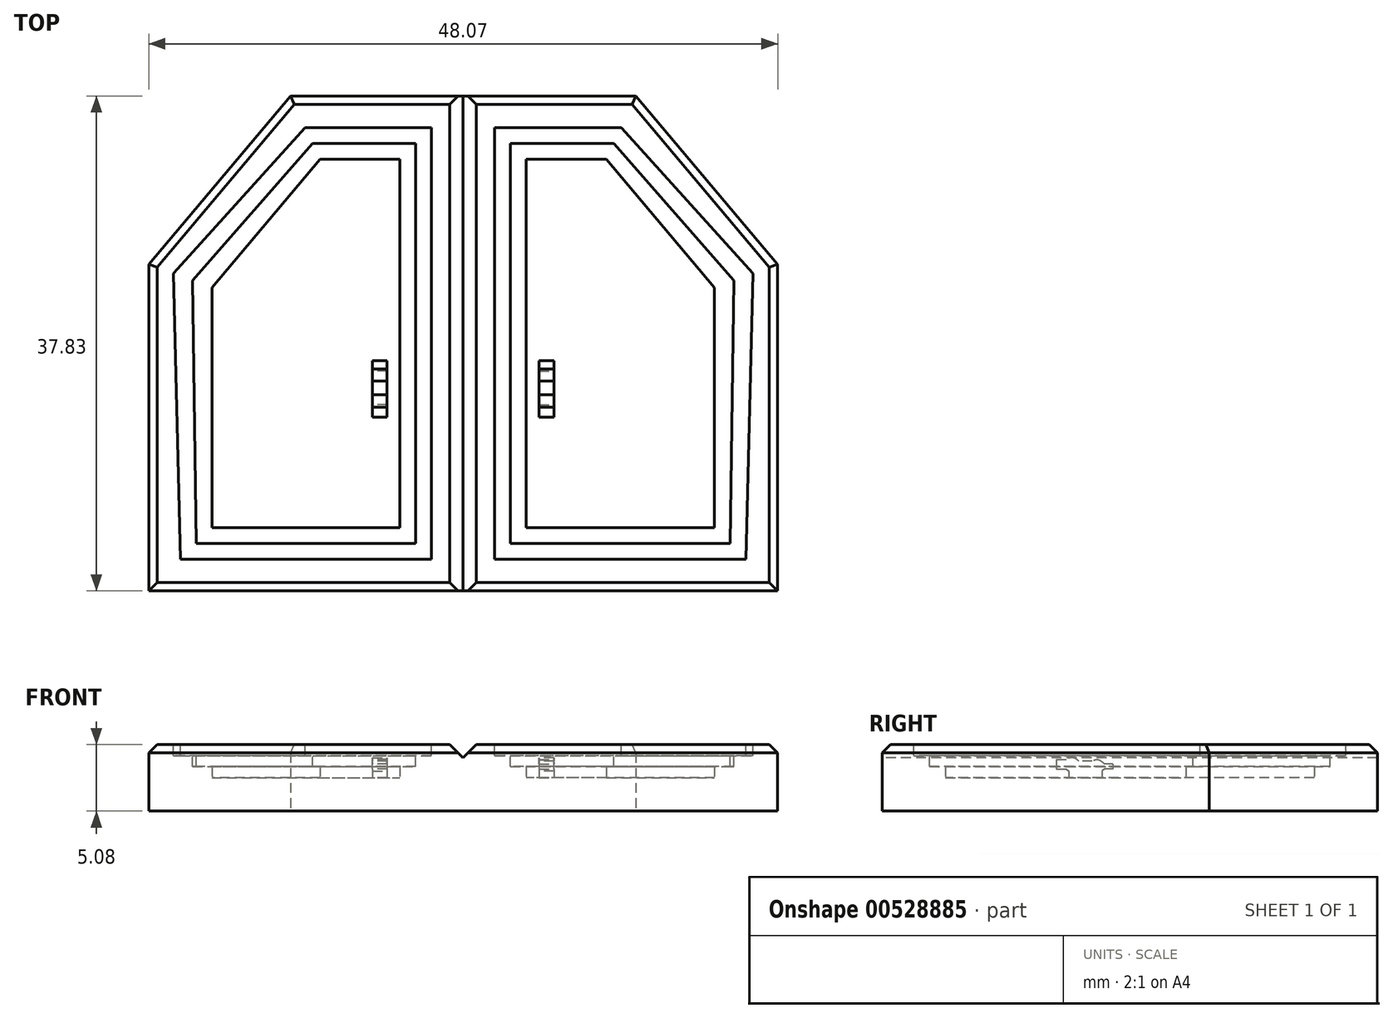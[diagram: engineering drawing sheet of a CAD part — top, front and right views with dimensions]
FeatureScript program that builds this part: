
annotation { "Feature Type Name" : "Feature", "Feature Type Description" : "" }
export const myFeature = defineFeature(function(context is Context, id is Id, definition is map)
    precondition{}
    {
        {
            var Q0;
            Q0=qCreatedBy(makeId("Top.planeOp"),FACE);
            var sketch = newSketch(context, id + "F0", { "sketchPlane" : qUnion([Q0])});
            skLineSegment(sketch, "E0.bottom", {"start": v(-36.19, -42.4) * mm, "end": v(13.77, -42.4) * mm});
            skLineSegment(sketch, "E0.top", {"start": v(-36.19, -4.56) * mm, "end": v(13.77, -4.56) * mm});
            skLineSegment(sketch, "E0.left", {"start": v(-36.19, -42.4) * mm, "end": v(-36.19, -4.56) * mm});
            skLineSegment(sketch, "E0.right", {"start": v(13.77, -42.4) * mm, "end": v(13.77, -4.56) * mm});
            skLineSegment(sketch, "E1", {"start": v(-11.2, -4.56) * mm, "end": v(-11.2, -42.4) * mm});
            skLineSegment(sketch, "E2", {"start": v(-12.16, -4.56) * mm, "end": v(-12.16, -42.4) * mm});
            skLineSegment(sketch, "E3", {"start": v(-25.35, -4.56) * mm, "end": v(-36.19, -17.43) * mm});
            skLineSegment(sketch, "E4", {"start": v(2.23, -4.56) * mm, "end": v(13.77, -17.77) * mm});
            skSolve(sketch);
        }
        {
            var Q0;
            {var subQ0=sQuery(id+"F0.wireOp",EDGE,"E2");Q0=makeQuery(id+"F0.imprint","IMPRINT",FACE,{"disambiguationData":[TD([[makeQuery(id+"F0.imprint","IMPRINT",EDGE,{"derivedFrom":subQ0}),-1.0]])]});}
            var Q1;
            {var subQ4=sQuery(id+"F0.wireOp",EDGE,"E1");Q1=makeQuery(id+"F0.imprint","IMPRINT",FACE,{"disambiguationData":[TD([[makeQuery(id+"F0.imprint","IMPRINT",EDGE,{"derivedFrom":subQ4}),1.0]])]});}
            extrude(context, id + "F1", {"entities" : qUnion([Q0, Q1]), "depth" : 5.08 * mm, "offsetDistance" : 25.4 * mm});
        }
        {
            var Q0;
            Q0=makeQuery(id+"F1.opExtrude","CAP_FACE",FACE,{"disambiguationData":[OSD([sQuery(id+"F0.wireOp",EDGE,"E0.bottom"),sQuery(id+"F0.wireOp",EDGE,"E0.top"),sQuery(id+"F0.wireOp",EDGE,"E0.left"),sQuery(id+"F0.wireOp",EDGE,"E2"),sQuery(id+"F0.wireOp",EDGE,"E3")])],"isStart":false});
            shell(context, id + "F2", {"entities" : qUnion([Q0]), "thickness" : 4.83 * mm});
        }
        {
            var Q0;
            Q0=makeQuery(id+"F2.opShell","OFFSET_FACE",FACE,{"disambiguationData":[OSD([sQuery(id+"F0.wireOp",EDGE,"E0.bottom"),sQuery(id+"F0.wireOp",EDGE,"E0.top"),sQuery(id+"F0.wireOp",EDGE,"E0.left"),sQuery(id+"F0.wireOp",EDGE,"E2"),sQuery(id+"F0.wireOp",EDGE,"E3")])]});
            extrude(context, id + "F3", {"entities" : qUnion([Q0]), "operationType" : NewBodyOperationType.REMOVE, "oppositeDirection" : true, "depth" : 2.54 * mm, "offsetDistance" : 25.4 * mm});
        }
        {
            var Q0;
            Q0=makeQuery(id+"F1.opExtrude","CAP_FACE",FACE,{"disambiguationData":[OSD([sQuery(id+"F0.wireOp",EDGE,"E0.bottom"),sQuery(id+"F0.wireOp",EDGE,"E0.top"),sQuery(id+"F0.wireOp",EDGE,"E0.left"),sQuery(id+"F0.wireOp",EDGE,"E2"),sQuery(id+"F0.wireOp",EDGE,"E3")])],"isStart":false});
            var sketch = newSketch(context, id + "F4", { "sketchPlane" : qUnion([Q0])});
            skLineSegment(sketch, "E5", {"start": v(-33.77, -39.98) * mm, "end": v(-14.57, -39.98) * mm});
            skLineSegment(sketch, "E6", {"start": v(-14.57, -39.98) * mm, "end": v(-14.57, -6.97) * mm});
            skLineSegment(sketch, "E7", {"start": v(-14.57, -6.97) * mm, "end": v(-24.22, -6.97) * mm});
            skLineSegment(sketch, "E8", {"start": v(-24.22, -6.97) * mm, "end": v(-34.3, -18.11) * mm});
            skLineSegment(sketch, "E9", {"start": v(-34.3, -18.11) * mm, "end": v(-33.77, -39.98) * mm});
            skSolve(sketch);
        }
        {
            var Q0;
            Q0=makeQuery(id+"F4.imprint","IMPRINT",FACE,{"disambiguationData":[TD([[makeQuery(id+"F4.imprint","IMPRINT",EDGE,{"derivedFrom":sQuery(id+"F4.wireOp",EDGE,"E5")}),1.0]])]});
            extrude(context, id + "F5", {"entities" : qUnion([Q0]), "operationType" : NewBodyOperationType.REMOVE, "oppositeDirection" : true, "depth" : 0.84 * mm, "offsetDistance" : 25.4 * mm});
        }
        {
            var Q0;
            Q0=makeQuery(id+"F5.boolean.opBoolean","COPY",FACE,{"derivedFrom":makeQuery(id+"F5.opExtrude","CAP_FACE",FACE,{"disambiguationData":[OSD([sQuery(id+"F0.wireOp",EDGE,"E0.bottom"),sQuery(id+"F0.wireOp",EDGE,"E0.top"),sQuery(id+"F0.wireOp",EDGE,"E0.left"),sQuery(id+"F0.wireOp",EDGE,"E2"),sQuery(id+"F0.wireOp",EDGE,"E3"),sQuery(id+"F4.wireOp",EDGE,"E5"),sQuery(id+"F4.wireOp",EDGE,"E6"),sQuery(id+"F4.wireOp",EDGE,"E7"),sQuery(id+"F4.wireOp",EDGE,"E8"),sQuery(id+"F4.wireOp",EDGE,"E9")])],"isStart":false})});
            var sketch = newSketch(context, id + "F6", { "sketchPlane" : qUnion([Q0])});
            skLineSegment(sketch, "E10", {"start": v(-23.66, -8.18) * mm, "end": v(-15.78, -8.18) * mm});
            skLineSegment(sketch, "E11", {"start": v(-15.78, -8.18) * mm, "end": v(-15.78, -38.78) * mm});
            skLineSegment(sketch, "E12", {"start": v(-15.78, -38.78) * mm, "end": v(-32.57, -38.78) * mm});
            skLineSegment(sketch, "E13", {"start": v(-32.57, -38.78) * mm, "end": v(-32.83, -18.65) * mm});
            skLineSegment(sketch, "E14", {"start": v(-32.83, -18.65) * mm, "end": v(-23.66, -8.18) * mm});
            skSolve(sketch);
        }
        {
            var Q0;
            Q0=makeQuery(id+"F6.imprint","IMPRINT",FACE,{"disambiguationData":[TD([[makeQuery(id+"F6.imprint","IMPRINT",EDGE,{"derivedFrom":sQuery(id+"F6.wireOp",EDGE,"E10")}),-1.0]])]});
            extrude(context, id + "F7", {"entities" : qUnion([Q0]), "operationType" : NewBodyOperationType.REMOVE, "oppositeDirection" : true, "depth" : 0.84 * mm, "offsetDistance" : 25.4 * mm});
        }
        {
            var Q0;
            Q0=makeQuery(id+"F3.boolean.opBoolean","COPY",FACE,{"derivedFrom":makeQuery(id+"F3.opExtrude","CAP_FACE",FACE,{"disambiguationData":[OSD([sQuery(id+"F0.wireOp",EDGE,"E0.bottom"),sQuery(id+"F0.wireOp",EDGE,"E0.top"),sQuery(id+"F0.wireOp",EDGE,"E0.left"),sQuery(id+"F0.wireOp",EDGE,"E2"),sQuery(id+"F0.wireOp",EDGE,"E3")])],"isStart":false})});
            extrude(context, id + "F8", {"entities" : qUnion([Q0]), "operationType" : NewBodyOperationType.ADD, "depth" : 0.25 * mm, "offsetDistance" : 25.4 * mm});
        }
        {
            var Q0;
            Q0=makeQuery(id+"F8.opExtrude","CAP_FACE",FACE,{"disambiguationData":[OSD([sQuery(id+"F0.wireOp",EDGE,"E0.bottom"),sQuery(id+"F0.wireOp",EDGE,"E0.top"),sQuery(id+"F0.wireOp",EDGE,"E0.left"),sQuery(id+"F0.wireOp",EDGE,"E2"),sQuery(id+"F0.wireOp",EDGE,"E3")])],"isStart":false});
            var sketch = newSketch(context, id + "F9", { "sketchPlane" : qUnion([Q0])});
            skLineSegment(sketch, "E15.bottom", {"start": v(-17.97, -25.6) * mm, "end": v(-19.08, -25.6) * mm});
            skLineSegment(sketch, "E15.top", {"start": v(-17.97, -28.16) * mm, "end": v(-19.08, -28.16) * mm});
            skLineSegment(sketch, "E15.left", {"start": v(-17.97, -25.6) * mm, "end": v(-17.97, -28.16) * mm});
            skLineSegment(sketch, "E15.right", {"start": v(-19.08, -25.6) * mm, "end": v(-19.08, -28.16) * mm});
            skSolve(sketch);
        }
        {
            var Q0;
            Q0=qSketchRegion(id+"F9",true);
            extrude(context, id + "F10", {"entities" : qUnion([Q0]), "operationType" : NewBodyOperationType.ADD, "depth" : 1.27 * mm, "offsetDistance" : 25.4 * mm});
        }
        {
            var Q0;
            Q0=makeQuery(id+"F10.opExtrude","CAP_EDGE",EDGE,{"disambiguationData":[OSD([sQuery(id+"F9.wireOp",EDGE,"E15.bottom")])],"isStart":false});
            var Q1;
            Q1=makeQuery(id+"F10.opExtrude","CAP_EDGE",EDGE,{"disambiguationData":[OSD([sQuery(id+"F9.wireOp",EDGE,"E15.top")])],"isStart":false});
            chamfer(context, id + "F11", {"entities" : qUnion([Q0, Q1]), "width" : 0.76 * mm, "tangentPropagation" : true});
        }
        {
            var Q0;
            Q0=makeQuery(id+"F11.opChamfer","BLEND_FACE",FACE,{"disambiguationData":[OSD([sQuery(id+"F9.wireOp",EDGE,"E15.top")])]});
            extrude(context, id + "F12", {"entities" : qUnion([Q0]), "operationType" : NewBodyOperationType.ADD, "depth" : 0.76 * mm, "offsetDistance" : 25.4 * mm});
        }
        {
            var Q0;
            Q0=makeQuery(id+"F12.opExtrude","CAP_EDGE",EDGE,{"disambiguationData":[OSD([sQuery(id+"F9.wireOp",EDGE,"E15.top")])],"isStart":false});
            chamfer(context, id + "F13", {"entities" : qUnion([Q0]), "width" : 0.5 * mm, "tangentPropagation" : true});
        }
        {
            var Q0;
            Q0=makeQuery(id+"F11.opChamfer","BLEND_FACE",FACE,{"disambiguationData":[OSD([sQuery(id+"F9.wireOp",EDGE,"E15.bottom")])]});
            extrude(context, id + "F14", {"entities" : qUnion([Q0]), "operationType" : NewBodyOperationType.ADD, "depth" : 0.5 * mm, "offsetDistance" : 25.4 * mm});
        }
        {
            var Q0;
            Q0=makeQuery(id+"F14.opExtrude","CAP_EDGE",EDGE,{"disambiguationData":[OSD([sQuery(id+"F9.wireOp",EDGE,"E15.bottom")])],"isStart":false});
            chamfer(context, id + "F15", {"entities" : qUnion([Q0]), "width" : 0.25 * mm, "tangentPropagation" : true});
        }
        {
            var Q0;
            Q0=makeQuery(id+"F15.opChamfer","BLEND_FACE",FACE,{"disambiguationData":[OSD([sQuery(id+"F9.wireOp",EDGE,"E15.bottom")])]});
            extrude(context, id + "F16", {"entities" : qUnion([Q0]), "operationType" : NewBodyOperationType.ADD, "depth" : 0.64 * mm, "offsetDistance" : 25.4 * mm});
        }
        {
            var Q0;
            Q0=makeQuery(id+"F13.opChamfer","BLEND_FACE",FACE,{"disambiguationData":[OSD([sQuery(id+"F9.wireOp",EDGE,"E15.top")])]});
            extrude(context, id + "F17", {"entities" : qUnion([Q0]), "operationType" : NewBodyOperationType.ADD, "depth" : 0.76 * mm, "offsetDistance" : 25.4 * mm});
        }
        {
            var Q0;
            Q0=makeQuery(id+"F12.opExtrude","CAP_EDGE",EDGE,{"disambiguationData":[OSD([sQuery(id+"F9.wireOp",EDGE,"E15.bottom"),sQuery(id+"F9.wireOp",EDGE,"E15.top"),sQuery(id+"F9.wireOp",EDGE,"E15.left"),sQuery(id+"F9.wireOp",EDGE,"E15.right")])],"isStart":false});
            var Q1;
            Q1=makeQuery(id+"F14.opExtrude","CAP_EDGE",EDGE,{"disambiguationData":[OSD([sQuery(id+"F9.wireOp",EDGE,"E15.bottom"),sQuery(id+"F9.wireOp",EDGE,"E15.top"),sQuery(id+"F9.wireOp",EDGE,"E15.left"),sQuery(id+"F9.wireOp",EDGE,"E15.right")])],"isStart":false});
            fillet(context, id + "F18", {"entities" : qUnion([Q0, Q1]), "radius" : 0.64 * mm, "tangentPropagation" : true, "allowEdgeOverflow" : false});
        }
        {
            var Q0;
            Q0=makeQuery(id+"F1.opExtrude","SWEPT_BODY",BODY,{"disambiguationData":[OSD([sQuery(id+"F0.wireOp",EDGE,"E0.bottom"),sQuery(id+"F0.wireOp",EDGE,"E0.top"),sQuery(id+"F0.wireOp",EDGE,"E0.right"),sQuery(id+"F0.wireOp",EDGE,"E1"),sQuery(id+"F0.wireOp",EDGE,"E4")])]});
            deleteBodies(context, id + "F19", {"entities" : qUnion([Q0])});
        }
        {
            var Q0;
            {var subQ0=sQuery(id+"F0.wireOp",EDGE,"E0.top");Q0=makeQuery(id+"F1.opExtrude","CAP_EDGE",EDGE,{"disambiguationData":[OSD([subQ0]),TDD([makeQuery(id+"F0.imprint","IMPRINT",EDGE,{"disambiguationData":[TD([[makeQuery(id+"F0.imprint","INTERSECT",VERTEX,{"derivedFrom":[subQ0,sQuery(id+"F0.wireOp",EDGE,"E2")]}),1.0]])],"derivedFrom":subQ0})])],"isStart":false});}
            var Q1;
            Q1=makeQuery(id+"F1.opExtrude","CAP_EDGE",EDGE,{"disambiguationData":[OSD([sQuery(id+"F0.wireOp",EDGE,"E3")])],"isStart":false});
            var Q2;
            Q2=makeQuery(id+"F1.opExtrude","CAP_EDGE",EDGE,{"disambiguationData":[OSD([sQuery(id+"F0.wireOp",EDGE,"E0.left")])],"isStart":false});
            var Q3;
            {var subQ0=sQuery(id+"F0.wireOp",EDGE,"E0.bottom");Q3=makeQuery(id+"F1.opExtrude","CAP_EDGE",EDGE,{"disambiguationData":[OSD([subQ0]),TDD([makeQuery(id+"F0.imprint","IMPRINT",EDGE,{"disambiguationData":[TD([[makeQuery(id+"F0.imprint","INTERSECT",VERTEX,{"derivedFrom":[subQ0,sQuery(id+"F0.wireOp",EDGE,"E0.left")]}),-1.0]])],"derivedFrom":subQ0})])],"isStart":false});}
            chamfer(context, id + "F20", {"entities" : qUnion([Q0, Q1, Q2, Q3]), "width" : 0.64 * mm, "tangentPropagation" : true});
        }
        {
            var Q0;
            Q0=makeQuery(id+"F1.opExtrude","CAP_EDGE",EDGE,{"disambiguationData":[OSD([sQuery(id+"F0.wireOp",EDGE,"E2")])],"isStart":false});
            chamfer(context, id + "F21", {"entities" : qUnion([Q0]), "width" : 1.02 * mm, "tangentPropagation" : true});
        }
        {
            var Q0;
            Q0=makeQuery(id+"F1.opExtrude","SWEPT_BODY",BODY,{"disambiguationData":[OSD([sQuery(id+"F0.wireOp",EDGE,"E0.bottom"),sQuery(id+"F0.wireOp",EDGE,"E0.top"),sQuery(id+"F0.wireOp",EDGE,"E0.left"),sQuery(id+"F0.wireOp",EDGE,"E2"),sQuery(id+"F0.wireOp",EDGE,"E3")])]});
            var Q1;
            Q1=makeQuery(id+"F1.opExtrude","SWEPT_FACE",FACE,{"disambiguationData":[OSD([sQuery(id+"F0.wireOp",EDGE,"E2")])]});
            mirror(context, id + "F22", {"operationType" : NewBodyOperationType.ADD, "entities" : qUnion([Q0]), "mirrorPlane" : qUnion([Q1])});
        }
    });
